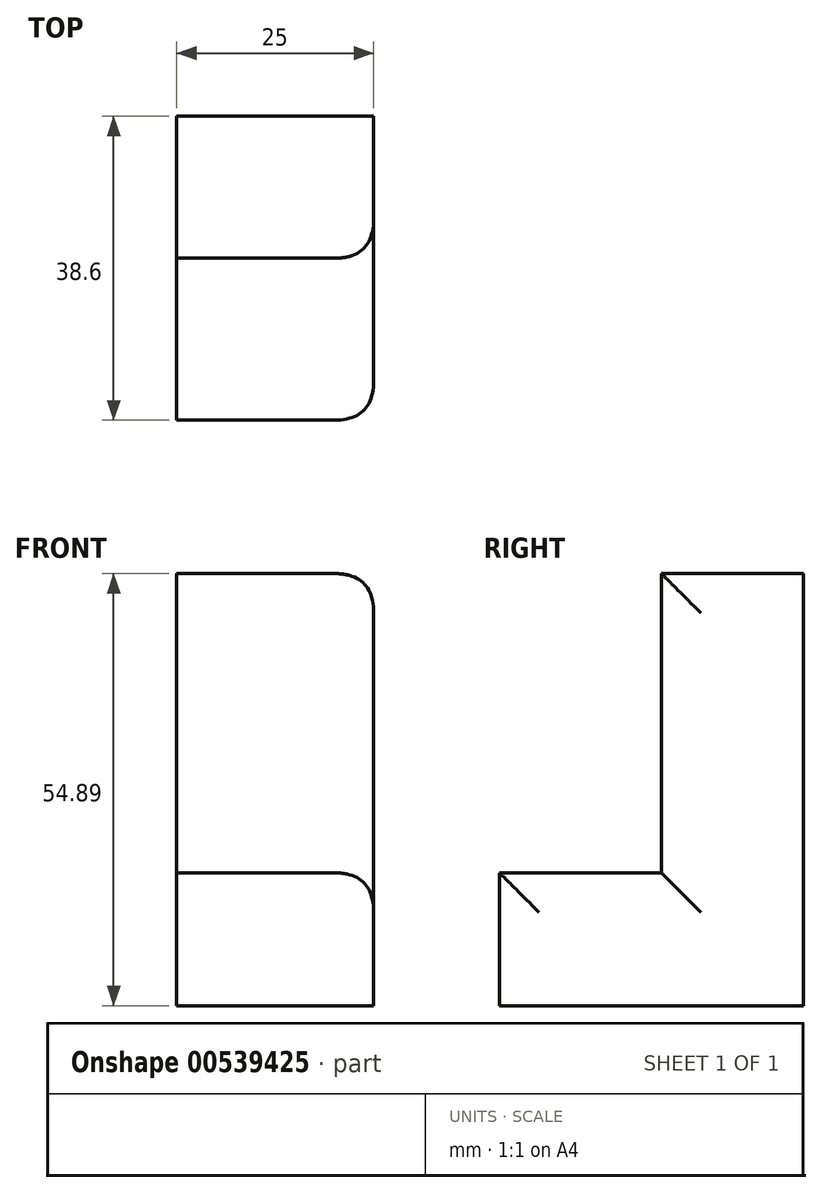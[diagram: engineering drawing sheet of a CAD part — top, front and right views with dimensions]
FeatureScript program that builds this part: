
annotation { "Feature Type Name" : "Feature", "Feature Type Description" : "" }
export const myFeature = defineFeature(function(context is Context, id is Id, definition is map)
    precondition{}
    {
        {
            var Q0;
            Q0=qCreatedBy(makeId("Right.planeOp"),FACE);
            var sketch = newSketch(context, id + "F0", { "sketchPlane" : qUnion([Q0])});
            skLineSegment(sketch, "E0", {"start": v(-38.6, 0) * mm, "end": v(0, 0) * mm});
            skLineSegment(sketch, "E1", {"start": v(0, 0) * mm, "end": v(0, 54.9) * mm});
            skLineSegment(sketch, "E2", {"start": v(-38.6, 0) * mm, "end": v(-38.6, 16.88) * mm});
            skLineSegment(sketch, "E3", {"start": v(-38.6, 16.88) * mm, "end": v(-18.04, 16.88) * mm});
            skLineSegment(sketch, "E4", {"start": v(-18.04, 16.88) * mm, "end": v(-18.04, 54.9) * mm});
            skLineSegment(sketch, "E5", {"start": v(-18.04, 54.9) * mm, "end": v(0, 54.9) * mm});
            skPoint(sketch, "E6.orphan", {"position": v(0, 55.86) * mm});
            skSolve(sketch);
        }
        {
            var Q0;
            Q0 = qSketchRegion(id + "F0", true);
            extrude(context, id + "F1", {"entities" : qUnion([Q0]), "depth" : 25 * mm, "offsetDistance" : 25 * mm});
        }
        {
            var Q0;
            Q0=makeQuery(id+"F1.opExtrude","CAP_EDGE",EDGE,{"disambiguationData":[OSD([sQuery(id+"F0.wireOp",EDGE,"E4")])],"isStart":false});
            var Q1;
            Q1=makeQuery(id+"F1.opExtrude","CAP_EDGE",EDGE,{"disambiguationData":[OSD([sQuery(id+"F0.wireOp",EDGE,"E5")])],"isStart":false});
            var Q2;
            Q2=makeQuery(id+"F1.opExtrude","CAP_EDGE",EDGE,{"disambiguationData":[OSD([sQuery(id+"F0.wireOp",EDGE,"E3")])],"isStart":false});
            var Q3;
            Q3=makeQuery(id+"F1.opExtrude","CAP_EDGE",EDGE,{"disambiguationData":[OSD([sQuery(id+"F0.wireOp",EDGE,"E2")])],"isStart":false});
            fillet(context, id + "F2", {"entities" : qUnion([Q0, Q1, Q2, Q3]), "radius" : 5 * mm, "tangentPropagation" : true, "rho" : 0.5, "crossSection" : FilletCrossSection.CONIC, "allowEdgeOverflow" : false});
        }
    });
